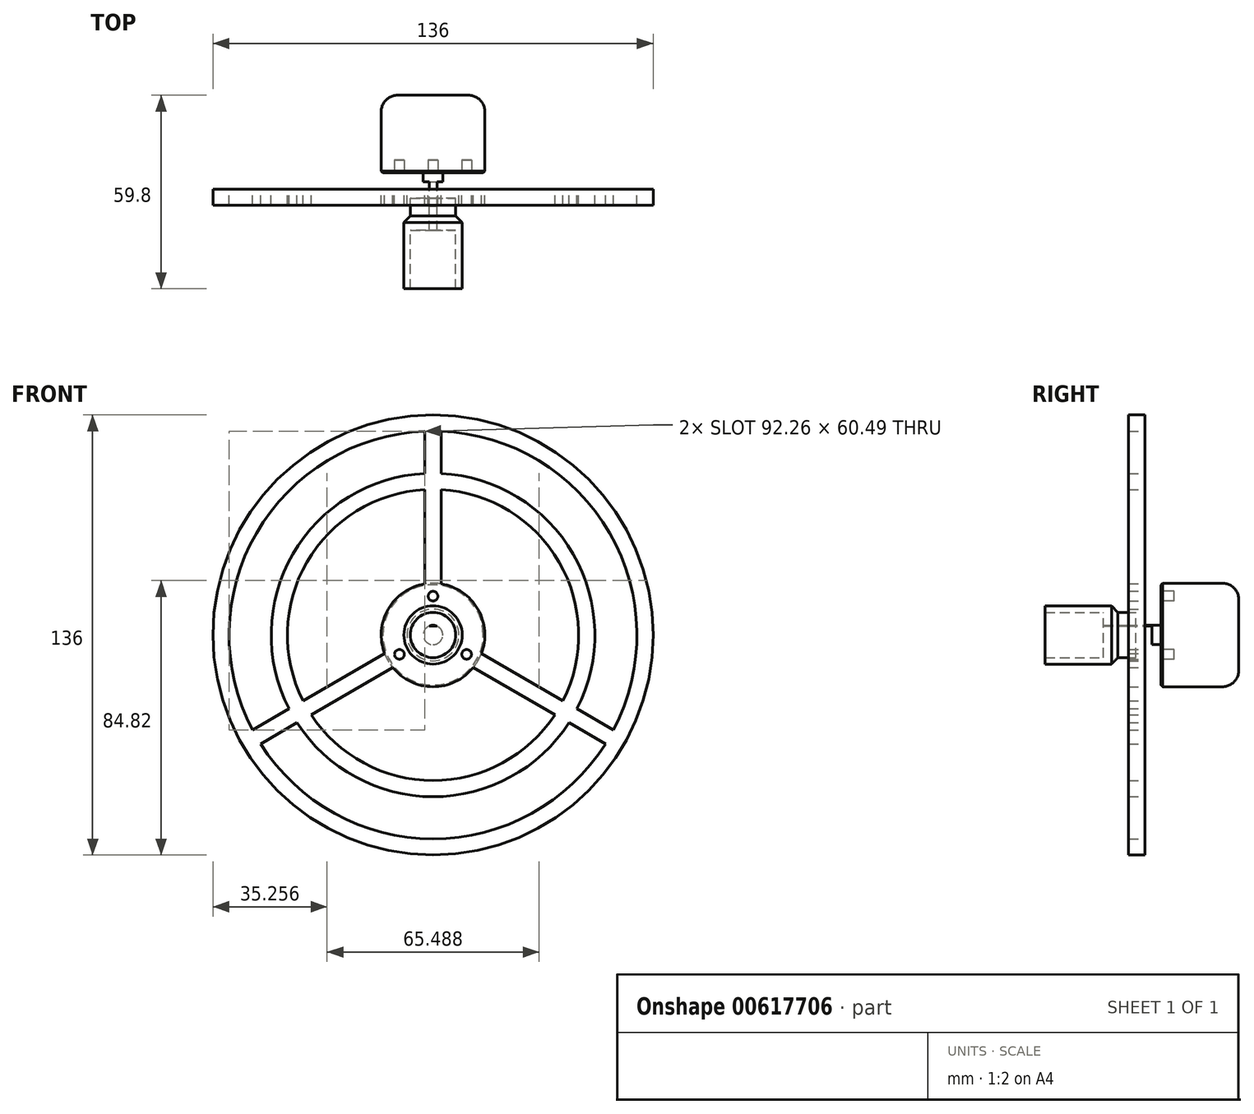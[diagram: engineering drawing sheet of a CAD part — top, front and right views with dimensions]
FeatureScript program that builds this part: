
annotation { "Feature Type Name" : "Feature", "Feature Type Description" : "" }
export const myFeature = defineFeature(function(context is Context, id is Id, definition is map)
    precondition{}
    {
        {
            var Q0;
            Q0=qCreatedBy(makeId("Front.planeOp"),FACE);
            var sketch = newSketch(context, id + "F0", { "sketchPlane" : qUnion([Q0])});
            skCircle(sketch, "E0", {"center": v(0, 0) * mm, "radius": 16 * mm});
            skCircle(sketch, "E1", {"center": v(0, 0) * mm, "radius": 8 * mm});
            skCircle(sketch, "E2", {"center": v(0, 0) * mm, "radius": 12 * mm, "construction": true});
            skLineSegment(sketch, "E3", {"start": v(0, 0) * mm, "end": v(0, 22.02) * mm, "construction": true});
            skLineSegment(sketch, "E4", {"start": v(0, 0) * mm, "end": v(-20.66, -11.93) * mm, "construction": true});
            skLineSegment(sketch, "E5", {"start": v(0, 0) * mm, "end": v(19.3, -11.14) * mm, "construction": true});
            skCircle(sketch, "E6", {"center": v(0, 12) * mm, "radius": 1.5 * mm});
            skCircle(sketch, "E7", {"center": v(10.4, -6) * mm, "radius": 1.5 * mm});
            skCircle(sketch, "E8", {"center": v(-10.4, -6) * mm, "radius": 1.5 * mm});
            skCircle(sketch, "E9", {"center": v(0, 0) * mm, "radius": 3 * mm});
            skLineSegment(sketch, "E10.bottom", {"start": v(-3.01, 2.75) * mm, "end": v(3.01, 2.75) * mm});
            skSolve(sketch);
        }
        {
            var Q0;
            Q0=makeQuery(id+"F0.imprint","IMPRINT",FACE,{"disambiguationData":[TD([[makeQuery(id+"F0.imprint","IMPRINT",EDGE,{"derivedFrom":sQuery(id+"F0.wireOp",EDGE,"E0")}),1.0]])]});
            var Q1;
            Q1=makeQuery(id+"F0.imprint","IMPRINT",FACE,{"disambiguationData":[TD([[makeQuery(id+"F0.imprint","IMPRINT",EDGE,{"derivedFrom":sQuery(id+"F0.wireOp",EDGE,"E1")}),1.0]])]});
            var Q2;
            Q2=makeQuery(id+"F0.imprint","IMPRINT",FACE,{"disambiguationData":[TD([[makeQuery(id+"F0.imprint","IMPRINT",EDGE,{"derivedFrom":sQuery(id+"F0.wireOp",EDGE,"E7")}),1.0]])]});
            var Q3;
            Q3=makeQuery(id+"F0.imprint","IMPRINT",FACE,{"disambiguationData":[TD([[makeQuery(id+"F0.imprint","IMPRINT",EDGE,{"derivedFrom":sQuery(id+"F0.wireOp",EDGE,"E8")}),1.0]])]});
            var Q4;
            Q4=makeQuery(id+"F0.imprint","IMPRINT",FACE,{"disambiguationData":[TD([[makeQuery(id+"F0.imprint","IMPRINT",EDGE,{"derivedFrom":sQuery(id+"F0.wireOp",EDGE,"E6")}),1.0]])]});
            var Q5;
            {var subQ0=sQuery(id+"F0.wireOp",EDGE,"E10.bottom");var subQ1=sQuery(id+"F0.wireOp",EDGE,"E9");var subQ2=makeQuery(id+"F0.imprint","INTERSECT",VERTEX,{"disambiguationData":[OD(0.0)],"derivedFrom":[subQ1,subQ0]});Q5=makeQuery(id+"F0.imprint","IMPRINT",FACE,{"disambiguationData":[TD([[makeQuery(id+"F0.imprint","IMPRINT",EDGE,{"disambiguationData":[TD([[subQ2,-1.0]])],"derivedFrom":subQ1}),1.0]])]});}
            var Q6;
            {var subQ0=sQuery(id+"F0.wireOp",EDGE,"E10.bottom");var subQ1=sQuery(id+"F0.wireOp",EDGE,"E9");var subQ2=makeQuery(id+"F0.imprint","INTERSECT",VERTEX,{"disambiguationData":[OD(0.0)],"derivedFrom":[subQ1,subQ0]});Q6=makeQuery(id+"F0.imprint","IMPRINT",FACE,{"disambiguationData":[TD([[makeQuery(id+"F0.imprint","IMPRINT",EDGE,{"disambiguationData":[TD([[subQ2,1.0]])],"derivedFrom":subQ1}),1.0]])]});}
            extrude(context, id + "F1", {"entities" : qUnion([Q0, Q1, Q2, Q3, Q4, Q5, Q6]), "oppositeDirection" : true, "depth" : 24 * mm, "offsetDistance" : 25 * mm});
        }
        {
            var Q0;
            Q0=makeQuery(id+"F0.imprint","IMPRINT",FACE,{"disambiguationData":[TD([[makeQuery(id+"F0.imprint","IMPRINT",EDGE,{"derivedFrom":sQuery(id+"F0.wireOp",EDGE,"E8")}),1.0]])]});
            var Q1;
            Q1=makeQuery(id+"F0.imprint","IMPRINT",FACE,{"disambiguationData":[TD([[makeQuery(id+"F0.imprint","IMPRINT",EDGE,{"derivedFrom":sQuery(id+"F0.wireOp",EDGE,"E6")}),1.0]])]});
            var Q2;
            Q2=makeQuery(id+"F0.imprint","IMPRINT",FACE,{"disambiguationData":[TD([[makeQuery(id+"F0.imprint","IMPRINT",EDGE,{"derivedFrom":sQuery(id+"F0.wireOp",EDGE,"E7")}),1.0]])]});
            var Q3;
            Q3=sQuery(id+"F0.wireOp",EDGE,"E6");
            var Q4;
            Q4=sQuery(id+"F0.wireOp",EDGE,"E7");
            var Q5;
            Q5=sQuery(id+"F0.wireOp",EDGE,"E8");
            extrude(context, id + "F2", {"entities" : qUnion([Q0, Q1, Q2]), "operationType" : NewBodyOperationType.REMOVE, "surfaceEntities" : qUnion([Q3, Q4, Q5]), "oppositeDirection" : true, "depth" : 4 * mm, "offsetDistance" : 25 * mm});
        }
        {
            var Q0;
            {var subQ0=sQuery(id+"F0.wireOp",EDGE,"E10.bottom");var subQ1=sQuery(id+"F0.wireOp",EDGE,"E9");var subQ2=makeQuery(id+"F0.imprint","INTERSECT",VERTEX,{"disambiguationData":[OD(0.0)],"derivedFrom":[subQ1,subQ0]});Q0=makeQuery(id+"F0.imprint","IMPRINT",FACE,{"disambiguationData":[TD([[makeQuery(id+"F0.imprint","IMPRINT",EDGE,{"disambiguationData":[TD([[subQ2,-1.0]])],"derivedFrom":subQ1}),1.0]])]});}
            var Q1;
            {var subQ0=sQuery(id+"F0.wireOp",EDGE,"E10.bottom");var subQ1=sQuery(id+"F0.wireOp",EDGE,"E9");var subQ2=makeQuery(id+"F0.imprint","INTERSECT",VERTEX,{"disambiguationData":[OD(0.0)],"derivedFrom":[subQ1,subQ0]});Q1=makeQuery(id+"F0.imprint","IMPRINT",FACE,{"disambiguationData":[TD([[makeQuery(id+"F0.imprint","IMPRINT",EDGE,{"disambiguationData":[TD([[subQ2,1.0]])],"derivedFrom":subQ1}),1.0]])]});}
            extrude(context, id + "F3", {"entities" : qUnion([Q0, Q1]), "operationType" : NewBodyOperationType.ADD, "depth" : 2.8 * mm, "offsetDistance" : 25 * mm});
        }
        {
            var Q0;
            Q0=makeQuery(id+"F3.opExtrude","CAP_FACE",FACE,{"disambiguationData":[OSD([sQuery(id+"F0.wireOp",EDGE,"E9")])],"isStart":false});
            var sketch = newSketch(context, id + "F4", { "sketchPlane" : qUnion([Q0])});
            skCircle(sketch, "E11", {"center": v(0, 0) * mm, "radius": 3 * mm});
            skLineSegment(sketch, "E12", {"start": v(-3.18, 2.75) * mm, "end": v(3.82, 2.75) * mm});
            skSolve(sketch);
        }
        {
            var Q0;
            {var subQ0=sQuery(id+"F4.wireOp",EDGE,"E12");var subQ1=sQuery(id+"F4.wireOp",EDGE,"E11");var subQ2=makeQuery(id+"F4.imprint","INTERSECT",VERTEX,{"disambiguationData":[OD(0.0)],"derivedFrom":[subQ1,subQ0]});Q0=makeQuery(id+"F4.imprint","IMPRINT",FACE,{"disambiguationData":[TD([[makeQuery(id+"F4.imprint","IMPRINT",EDGE,{"disambiguationData":[TD([[subQ2,-1.0]])],"derivedFrom":subQ1}),1.0]])]});}
            extrude(context, id + "F5", {"entities" : qUnion([Q0]), "operationType" : NewBodyOperationType.ADD, "depth" : 7.5 * mm, "offsetDistance" : 25 * mm});
        }
        {
            var Q0;
            Q0=makeQuery(id+"F1.opExtrude","CAP_EDGE",EDGE,{"disambiguationData":[OSD([sQuery(id+"F0.wireOp",EDGE,"E0")])],"isStart":false});
            fillet(context, id + "F6", {"entities" : qUnion([Q0]), "radius" : 5 * mm, "tangentPropagation" : true, "allowEdgeOverflow" : false});
        }
        {
            var Q0;
            Q0=makeQuery(id+"F1.opExtrude","CAP_EDGE",EDGE,{"disambiguationData":[OSD([sQuery(id+"F0.wireOp",EDGE,"E0")])],"isStart":true});
            chamfer(context, id + "F7", {"entities" : qUnion([Q0]), "width" : 0.5 * mm, "tangentPropagation" : true});
        }
        {
            var Q0;
            Q0=makeQuery(id+"F3.opExtrude","CAP_FACE",FACE,{"disambiguationData":[OSD([sQuery(id+"F0.wireOp",EDGE,"E9"),sQuery(id+"F0.wireOp",EDGE,"E10.bottom")])],"isStart":false});
            var sketch = newSketch(context, id + "F8", { "sketchPlane" : qUnion([Q0])});
            skCircle(sketch, "E13", {"center": v(0, 0) * mm, "radius": 7 * mm});
            skCircle(sketch, "E14", {"center": v(0, 0) * mm, "radius": 3 * mm});
            skLineSegment(sketch, "E15", {"start": v(-2.98, 2.75) * mm, "end": v(3.76, 2.75) * mm});
            skSolve(sketch);
        }
        {
            var Q0;
            Q0=makeQuery(id+"F8.imprint","IMPRINT",FACE,{"disambiguationData":[TD([[makeQuery(id+"F8.imprint","IMPRINT",EDGE,{"derivedFrom":sQuery(id+"F8.wireOp",EDGE,"E13")}),1.0]])]});
            var Q1;
            {var subQ0=sQuery(id+"F8.wireOp",EDGE,"E15");var subQ1=sQuery(id+"F8.wireOp",EDGE,"E14");var subQ2=makeQuery(id+"F8.imprint","INTERSECT",VERTEX,{"disambiguationData":[OD(0.0)],"derivedFrom":[subQ1,subQ0]});Q1=makeQuery(id+"F8.imprint","IMPRINT",FACE,{"disambiguationData":[TD([[makeQuery(id+"F8.imprint","IMPRINT",EDGE,{"disambiguationData":[TD([[subQ2,1.0]])],"derivedFrom":subQ1}),1.0]])]});}
            var Q2;
            Q2=sQuery(id+"F8.wireOp",EDGE,"E13");
            extrude(context, id + "F9", {"entities" : qUnion([Q0, Q1]), "surfaceEntities" : qUnion([Q2]), "depth" : 15 * mm, "offsetDistance" : 25 * mm, "hasSecondDirection" : true, "secondDirectionOppositeDirection" : true, "secondDirectionDepth" : -5 * mm});
        }
        {
            var Q0;
            Q0=makeQuery(id+"F9.opExtrude","CAP_FACE",FACE,{"disambiguationData":[OSD([sQuery(id+"F0.wireOp",EDGE,"E9"),sQuery(id+"F0.wireOp",EDGE,"E10.bottom"),sQuery(id+"F8.wireOp",EDGE,"E13")])],"isStart":false});
            var sketch = newSketch(context, id + "F10", { "sketchPlane" : qUnion([Q0])});
            skCircle(sketch, "E16", {"center": v(0, 0) * mm, "radius": 9 * mm});
            skSolve(sketch);
        }
        {
            var Q0;
            Q0=makeQuery(id+"F10.imprint","IMPRINT",FACE,{"disambiguationData":[TD([[makeQuery(id+"F10.imprint","IMPRINT",EDGE,{"derivedFrom":sQuery(id+"F10.wireOp",EDGE,"E16")}),1.0]])]});
            extrude(context, id + "F11", {"entities" : qUnion([Q0]), "operationType" : NewBodyOperationType.ADD, "depth" : 18 * mm, "offsetDistance" : 25 * mm, "hasSecondDirection" : true, "secondDirectionOppositeDirection" : true, "secondDirectionDepth" : 5 * mm});
        }
        {
            var Q0;
            Q0=makeQuery(id+"F11.opExtrude","CAP_EDGE",EDGE,{"disambiguationData":[OSD([sQuery(id+"F10.wireOp",EDGE,"E16")])],"isStart":true});
            chamfer(context, id + "F12", {"entities" : qUnion([Q0]), "width" : 2.5 * mm, "tangentPropagation" : true});
        }
        {
            var Q0;
            Q0=makeQuery(id+"F1.opExtrude","CAP_FACE",FACE,{"disambiguationData":[OSD([sQuery(id+"F0.wireOp",EDGE,"E0")])],"isStart":true});
            cPlane(context, id + "F13", {"entities" : qUnion([Q0]), "cplaneType" : CPlaneType.OFFSET, "offset" : 5 * mm, "width" : 150 * mm, "height" : 150 * mm});
        }
        {
            var Q0;
            Q0=qCreatedBy(id+"F13.planeOp",FACE);
            var sketch = newSketch(context, id + "F14", { "sketchPlane" : qUnion([Q0])});
            skCircle(sketch, "E17", {"center": v(0, 0) * mm, "radius": 16 * mm});
            skCircle(sketch, "E18", {"center": v(0, 0) * mm, "radius": 8 * mm});
            skCircle(sketch, "E19", {"center": v(0, 0) * mm, "radius": 12 * mm, "construction": true});
            skLineSegment(sketch, "E20", {"start": v(0, 0) * mm, "end": v(0, 18.9) * mm, "construction": true});
            skLineSegment(sketch, "E21", {"start": v(0, 0) * mm, "end": v(-20.66, -11.93) * mm, "construction": true});
            skLineSegment(sketch, "E22", {"start": v(0, 0) * mm, "end": v(19.3, -11.14) * mm, "construction": true});
            skCircle(sketch, "E23", {"center": v(0, 12) * mm, "radius": 1.5 * mm});
            skCircle(sketch, "E24", {"center": v(10.4, -6) * mm, "radius": 1.5 * mm});
            skCircle(sketch, "E25", {"center": v(-10.4, -6) * mm, "radius": 1.5 * mm});
            skCircle(sketch, "E26", {"center": v(0, 0) * mm, "radius": 3 * mm});
            skLineSegment(sketch, "E27.bottom", {"start": v(-3.01, 2.75) * mm, "end": v(3.01, 2.75) * mm});
            skLineSegment(sketch, "E28", {"start": v(-2.5, 65.94) * mm, "end": v(-2.5, 7.6) * mm});
            skLineSegment(sketch, "E29", {"start": v(2.5, 65.94) * mm, "end": v(2.5, 7.6) * mm});
            skLineSegment(sketch, "E30", {"start": v(7.83, -1.63) * mm, "end": v(58.36, -30.8) * mm});
            skLineSegment(sketch, "E31", {"start": v(5.33, -5.96) * mm, "end": v(55.86, -35.13) * mm});
            skLineSegment(sketch, "E32", {"start": v(-5.33, -5.96) * mm, "end": v(-55.86, -35.13) * mm});
            skLineSegment(sketch, "E33", {"start": v(-7.83, -1.63) * mm, "end": v(-58.36, -30.8) * mm});
            skLineSegment(sketch, "E34", {"start": v(-2.5, 65.94) * mm, "end": v(2.5, 65.94) * mm});
            skLineSegment(sketch, "E35", {"start": v(58.36, -30.8) * mm, "end": v(55.86, -35.13) * mm});
            skLineSegment(sketch, "E36", {"start": v(-55.86, -35.13) * mm, "end": v(-58.36, -30.8) * mm});
            skCircle(sketch, "E37", {"center": v(0, 0) * mm, "radius": 63 * mm});
            skCircle(sketch, "E38", {"center": v(0, 0) * mm, "radius": 50 * mm});
            skCircle(sketch, "E39", {"center": v(0, 0) * mm, "radius": 45 * mm});
            skCircle(sketch, "E40", {"center": v(0, 0) * mm, "radius": 68 * mm});
            skSolve(sketch);
        }
        {
            var Q0;
            {var subQ5=sQuery(id+"F14.wireOp",EDGE,"E34");Q0=makeQuery(id+"F14.imprint","IMPRINT",FACE,{"disambiguationData":[TD([[makeQuery(id+"F14.imprint","IMPRINT",EDGE,{"derivedFrom":subQ5}),-1.0]])]});}
            var Q1;
            Q1=makeQuery(id+"F14.imprint","IMPRINT",FACE,{"disambiguationData":[TD([[makeQuery(id+"F14.imprint","IMPRINT",EDGE,{"derivedFrom":sQuery(id+"F14.wireOp",EDGE,"E23")}),-1.0]])]});
            var Q2;
            {var subQ0=sQuery(id+"F14.wireOp",EDGE,"E29");var subQ1=sQuery(id+"F14.wireOp",EDGE,"E17");var subQ2=makeQuery(id+"F14.imprint","INTERSECT",VERTEX,{"derivedFrom":[subQ1,subQ0]});Q2=makeQuery(id+"F14.imprint","IMPRINT",FACE,{"disambiguationData":[TD([[makeQuery(id+"F14.imprint","IMPRINT",EDGE,{"disambiguationData":[TD([[subQ2,1.0]])],"derivedFrom":subQ1}),1.0]])]});}
            var Q3;
            {var subQ0=sQuery(id+"F14.wireOp",EDGE,"E28");var subQ1=sQuery(id+"F14.wireOp",EDGE,"E17");var subQ2=makeQuery(id+"F14.imprint","INTERSECT",VERTEX,{"derivedFrom":[subQ1,subQ0]});Q3=makeQuery(id+"F14.imprint","IMPRINT",FACE,{"disambiguationData":[TD([[makeQuery(id+"F14.imprint","IMPRINT",EDGE,{"disambiguationData":[TD([[subQ2,-1.0]])],"derivedFrom":subQ1}),1.0]])]});}
            var Q4;
            Q4=makeQuery(id+"F14.imprint","IMPRINT",FACE,{"disambiguationData":[TD([[makeQuery(id+"F14.imprint","IMPRINT",EDGE,{"derivedFrom":sQuery(id+"F14.wireOp",EDGE,"E25")}),-1.0]])]});
            var Q5;
            {var subQ5=sQuery(id+"F14.wireOp",EDGE,"E36");Q5=makeQuery(id+"F14.imprint","IMPRINT",FACE,{"disambiguationData":[TD([[makeQuery(id+"F14.imprint","IMPRINT",EDGE,{"derivedFrom":subQ5}),-1.0]])]});}
            var Q6;
            {var subQ0=sQuery(id+"F14.wireOp",EDGE,"E32");var subQ1=sQuery(id+"F14.wireOp",EDGE,"E17");var subQ2=makeQuery(id+"F14.imprint","INTERSECT",VERTEX,{"derivedFrom":[subQ1,subQ0]});Q6=makeQuery(id+"F14.imprint","IMPRINT",FACE,{"disambiguationData":[TD([[makeQuery(id+"F14.imprint","IMPRINT",EDGE,{"disambiguationData":[TD([[subQ2,-1.0]])],"derivedFrom":subQ1}),1.0]])]});}
            var Q7;
            {var subQ5=sQuery(id+"F14.wireOp",EDGE,"E35");Q7=makeQuery(id+"F14.imprint","IMPRINT",FACE,{"disambiguationData":[TD([[makeQuery(id+"F14.imprint","IMPRINT",EDGE,{"derivedFrom":subQ5}),-1.0]])]});}
            var Q8;
            Q8=makeQuery(id+"F14.imprint","IMPRINT",FACE,{"disambiguationData":[TD([[makeQuery(id+"F14.imprint","IMPRINT",EDGE,{"derivedFrom":sQuery(id+"F14.wireOp",EDGE,"E24")}),-1.0]])]});
            var Q9;
            {var subQ9=sQuery(id+"F14.wireOp",EDGE,"E34");Q9=makeQuery(id+"F14.imprint","IMPRINT",FACE,{"disambiguationData":[TD([[makeQuery(id+"F14.imprint","IMPRINT",EDGE,{"derivedFrom":subQ9}),1.0]])]});}
            var Q10;
            {var subQ0=sQuery(id+"F14.wireOp",EDGE,"E38");var subQ1=sQuery(id+"F14.wireOp",EDGE,"E28");var subQ2=makeQuery(id+"F14.imprint","INTERSECT",VERTEX,{"derivedFrom":[subQ1,subQ0]});Q10=makeQuery(id+"F14.imprint","IMPRINT",FACE,{"disambiguationData":[TD([[makeQuery(id+"F14.imprint","IMPRINT",EDGE,{"disambiguationData":[TD([[subQ2,-1.0]])],"derivedFrom":subQ1}),-1.0]])]});}
            var Q11;
            {var subQ0=sQuery(id+"F14.wireOp",EDGE,"E39");var subQ1=sQuery(id+"F14.wireOp",EDGE,"E32");var subQ2=makeQuery(id+"F14.imprint","INTERSECT",VERTEX,{"derivedFrom":[subQ1,subQ0]});Q11=makeQuery(id+"F14.imprint","IMPRINT",FACE,{"disambiguationData":[TD([[makeQuery(id+"F14.imprint","IMPRINT",EDGE,{"disambiguationData":[TD([[subQ2,-1.0]])],"derivedFrom":subQ1}),-1.0]])]});}
            var Q12;
            {var subQ0=sQuery(id+"F14.wireOp",EDGE,"E33");var subQ1=sQuery(id+"F14.wireOp",EDGE,"E17");var subQ2=makeQuery(id+"F14.imprint","INTERSECT",VERTEX,{"derivedFrom":[subQ1,subQ0]});Q12=makeQuery(id+"F14.imprint","IMPRINT",FACE,{"disambiguationData":[TD([[makeQuery(id+"F14.imprint","IMPRINT",EDGE,{"disambiguationData":[TD([[subQ2,-1.0]])],"derivedFrom":subQ1}),-1.0]])]});}
            var Q13;
            {var subQ0=sQuery(id+"F14.wireOp",EDGE,"E38");var subQ1=sQuery(id+"F14.wireOp",EDGE,"E32");var subQ2=makeQuery(id+"F14.imprint","INTERSECT",VERTEX,{"derivedFrom":[subQ1,subQ0]});Q13=makeQuery(id+"F14.imprint","IMPRINT",FACE,{"disambiguationData":[TD([[makeQuery(id+"F14.imprint","IMPRINT",EDGE,{"disambiguationData":[TD([[subQ2,-1.0]])],"derivedFrom":subQ1}),-1.0]])]});}
            var Q14;
            {var subQ0=sQuery(id+"F14.wireOp",EDGE,"E39");var subQ1=sQuery(id+"F14.wireOp",EDGE,"E31");var subQ2=makeQuery(id+"F14.imprint","INTERSECT",VERTEX,{"derivedFrom":[subQ1,subQ0]});Q14=makeQuery(id+"F14.imprint","IMPRINT",FACE,{"disambiguationData":[TD([[makeQuery(id+"F14.imprint","IMPRINT",EDGE,{"disambiguationData":[TD([[subQ2,-1.0]])],"derivedFrom":subQ1}),-1.0]])]});}
            var Q15;
            {var subQ0=sQuery(id+"F14.wireOp",EDGE,"E31");var subQ1=sQuery(id+"F14.wireOp",EDGE,"E17");var subQ2=makeQuery(id+"F14.imprint","INTERSECT",VERTEX,{"derivedFrom":[subQ1,subQ0]});Q15=makeQuery(id+"F14.imprint","IMPRINT",FACE,{"disambiguationData":[TD([[makeQuery(id+"F14.imprint","IMPRINT",EDGE,{"disambiguationData":[TD([[subQ2,-1.0]])],"derivedFrom":subQ1}),-1.0]])]});}
            var Q16;
            {var subQ0=sQuery(id+"F14.wireOp",EDGE,"E38");var subQ1=sQuery(id+"F14.wireOp",EDGE,"E30");var subQ2=makeQuery(id+"F14.imprint","INTERSECT",VERTEX,{"derivedFrom":[subQ1,subQ0]});Q16=makeQuery(id+"F14.imprint","IMPRINT",FACE,{"disambiguationData":[TD([[makeQuery(id+"F14.imprint","IMPRINT",EDGE,{"disambiguationData":[TD([[subQ2,-1.0]])],"derivedFrom":subQ1}),-1.0]])]});}
            var Q17;
            {var subQ0=sQuery(id+"F14.wireOp",EDGE,"E38");var subQ1=sQuery(id+"F14.wireOp",EDGE,"E29");var subQ2=makeQuery(id+"F14.imprint","INTERSECT",VERTEX,{"derivedFrom":[subQ1,subQ0]});Q17=makeQuery(id+"F14.imprint","IMPRINT",FACE,{"disambiguationData":[TD([[makeQuery(id+"F14.imprint","IMPRINT",EDGE,{"disambiguationData":[TD([[subQ2,-1.0]])],"derivedFrom":subQ1}),1.0]])]});}
            var Q18;
            {var subQ0=sQuery(id+"F14.wireOp",EDGE,"E28");var subQ1=sQuery(id+"F14.wireOp",EDGE,"E17");var subQ2=makeQuery(id+"F14.imprint","INTERSECT",VERTEX,{"derivedFrom":[subQ1,subQ0]});Q18=makeQuery(id+"F14.imprint","IMPRINT",FACE,{"disambiguationData":[TD([[makeQuery(id+"F14.imprint","IMPRINT",EDGE,{"disambiguationData":[TD([[subQ2,1.0]])],"derivedFrom":subQ1}),-1.0]])]});}
            var Q19;
            {var subQ0=sQuery(id+"F14.wireOp",EDGE,"E39");var subQ1=sQuery(id+"F14.wireOp",EDGE,"E30");var subQ2=makeQuery(id+"F14.imprint","INTERSECT",VERTEX,{"derivedFrom":[subQ1,subQ0]});Q19=makeQuery(id+"F14.imprint","IMPRINT",FACE,{"disambiguationData":[TD([[makeQuery(id+"F14.imprint","IMPRINT",EDGE,{"disambiguationData":[TD([[subQ2,-1.0]])],"derivedFrom":subQ1}),-1.0]])]});}
            var Q20;
            {var subQ0=sQuery(id+"F14.wireOp",EDGE,"E38");var subQ1=sQuery(id+"F14.wireOp",EDGE,"E28");var subQ2=makeQuery(id+"F14.imprint","INTERSECT",VERTEX,{"derivedFrom":[subQ1,subQ0]});Q20=makeQuery(id+"F14.imprint","IMPRINT",FACE,{"disambiguationData":[TD([[makeQuery(id+"F14.imprint","IMPRINT",EDGE,{"disambiguationData":[TD([[subQ2,-1.0]])],"derivedFrom":subQ1}),1.0]])]});}
            var Q21;
            {var subQ0=sQuery(id+"F14.wireOp",EDGE,"E37");var subQ1=sQuery(id+"F14.wireOp",EDGE,"E28");var subQ2=makeQuery(id+"F14.imprint","INTERSECT",VERTEX,{"derivedFrom":[subQ1,subQ0]});Q21=makeQuery(id+"F14.imprint","IMPRINT",FACE,{"disambiguationData":[TD([[makeQuery(id+"F14.imprint","IMPRINT",EDGE,{"disambiguationData":[TD([[subQ2,-1.0]])],"derivedFrom":subQ1}),1.0]])]});}
            extrude(context, id + "F15", {"entities" : qUnion([Q0, Q1, Q2, Q3, Q4, Q5, Q6, Q7, Q8, Q9, Q10, Q11, Q12, Q13, Q14, Q15, Q16, Q17, Q18, Q19, Q20, Q21]), "depth" : 5 * mm, "offsetDistance" : 25 * mm});
        }
    });
